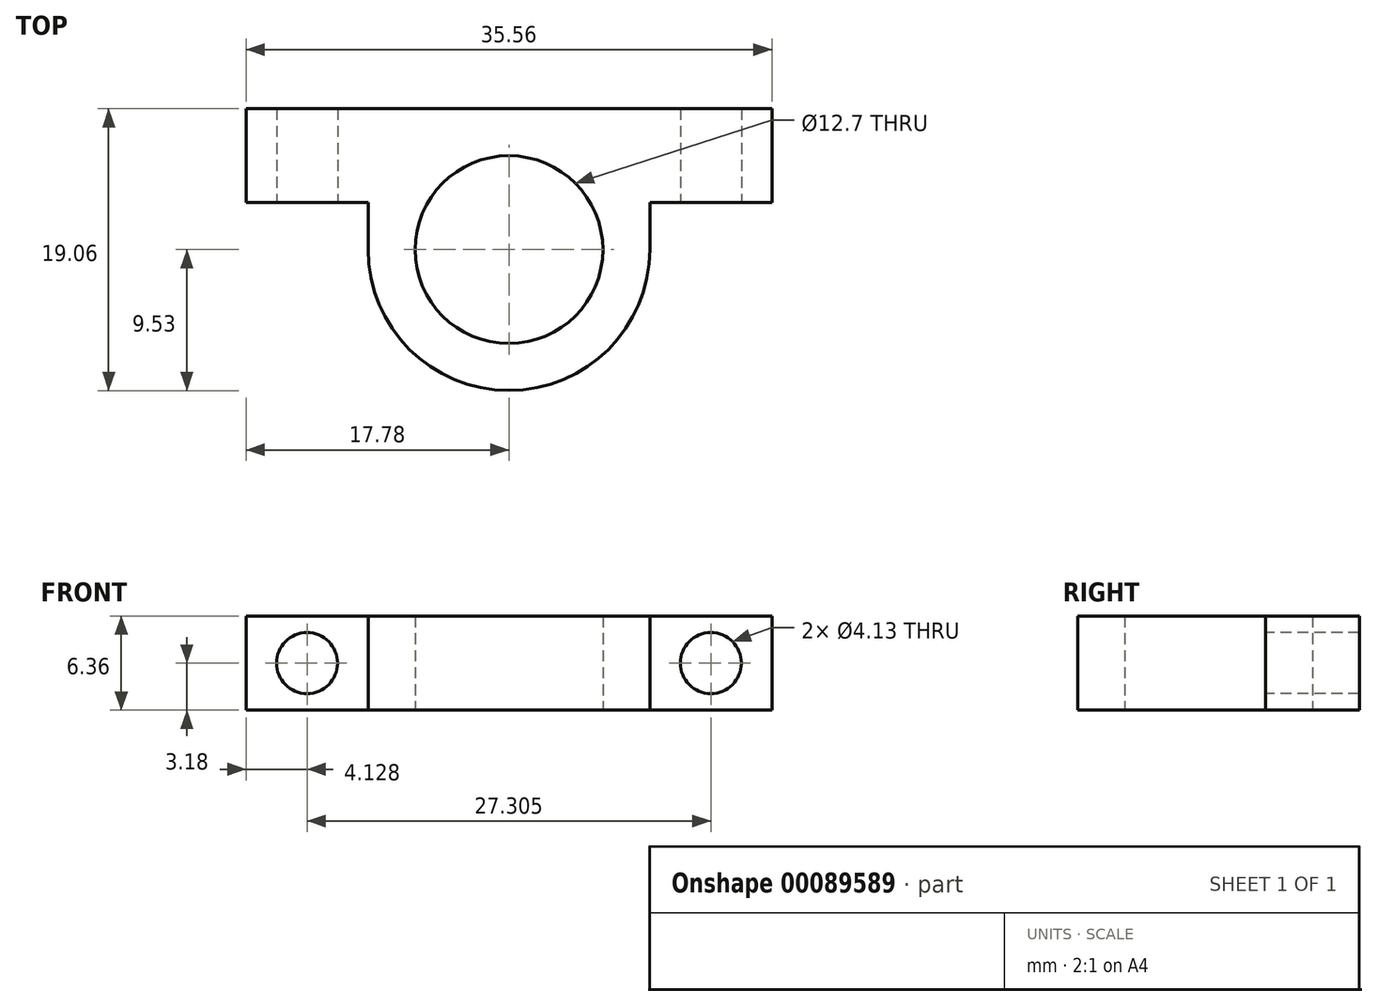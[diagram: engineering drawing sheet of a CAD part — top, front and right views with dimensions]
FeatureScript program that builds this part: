
annotation { "Feature Type Name" : "Feature", "Feature Type Description" : "" }
export const myFeature = defineFeature(function(context is Context, id is Id, definition is map)
    precondition{}
    {
        {
            var Q0;
            Q0=qCreatedBy(makeId("Top.planeOp"),FACE);
            var sketch = newSketch(context, id + "F0", { "sketchPlane" : qUnion([Q0])});
            skCircle(sketch, "E0", {"center": v(0, 0) * mm, "radius": 6.35 * mm});
            skArc(sketch, "E1", {"start": v(-9.53, 0) * mm, "mid": v(0, -9.53) * mm, "end": v(9.53, 0) * mm});
            skLineSegment(sketch, "E2", {"start": v(-9.53, 0) * mm, "end": v(-9.53, 3.17) * mm});
            skLineSegment(sketch, "E3", {"start": v(-9.53, 3.17) * mm, "end": v(-17.78, 3.17) * mm});
            skLineSegment(sketch, "E4", {"start": v(-17.78, 3.17) * mm, "end": v(-17.78, 9.53) * mm});
            skLineSegment(sketch, "E5.MirrorCS", {"start": v(17.78, 3.17) * mm, "end": v(17.78, 9.53) * mm});
            skLineSegment(sketch, "E6.MirrorCS", {"start": v(9.53, 3.18) * mm, "end": v(17.78, 3.18) * mm});
            skLineSegment(sketch, "E7.MirrorCS", {"start": v(9.53, 0) * mm, "end": v(9.53, 3.17) * mm});
            skLineSegment(sketch, "E8", {"start": v(-17.78, 9.52) * mm, "end": v(17.78, 9.53) * mm});
            skPoint(sketch, "E9", {"position": v(-9.53, 9.52) * mm});
            skPoint(sketch, "E10", {"position": v(-13.65, 9.52) * mm});
            skPoint(sketch, "E10.positionSnap0", {"position": v(-13.65, 3.17) * mm});
            skPoint(sketch, "E11", {"position": v(13.65, 9.53) * mm});
            skPoint(sketch, "E11.positionSnap0", {"position": v(13.65, 3.18) * mm});
            skSolve(sketch);
        }
        {
            var Q0;
            Q0=makeQuery(id+"F0.imprint","IMPRINT",FACE,{"disambiguationData":[TD([[makeQuery(id+"F0.imprint","IMPRINT",EDGE,{"derivedFrom":sQuery(id+"F0.wireOp",EDGE,"E0")}),-1.0]])]});
            extrude(context, id + "F1", {"entities" : qUnion([Q0]), "endBound" : BoundingType.SYMMETRIC, "depth" : 6.35 * mm});
        }
        {
            var Q0;
            Q0=makeQuery(id+"F1.opExtrude","SWEPT_FACE",FACE,{"disambiguationData":[OSD([sQuery(id+"F0.wireOp",EDGE,"E3")])]});
            var sketch = newSketch(context, id + "F2", { "sketchPlane" : qUnion([Q0])});
            skLineSegment(sketch, "E12", {"start": v(-13.65, 3.18) * mm, "end": v(-13.65, -3.18) * mm, "construction": true});
            skCircle(sketch, "E13", {"center": v(-13.65, 0) * mm, "radius": 2.06 * mm});
            skSolve(sketch);
        }
        {
            var Q0;
            Q0=qSketchRegion(id+"F2",true);
            extrude(context, id + "F3", {"entities" : qUnion([Q0]), "operationType" : NewBodyOperationType.REMOVE, "endBound" : BoundingType.THROUGH_ALL, "oppositeDirection" : true, "depth" : 25.4 * mm});
        }
        {
            var Q0;
            Q0=makeQuery(id+"F1.opExtrude","SWEPT_FACE",FACE,{"disambiguationData":[OSD([sQuery(id+"F0.wireOp",EDGE,"E6.MirrorCS")])]});
            var sketch = newSketch(context, id + "F4", { "sketchPlane" : qUnion([Q0])});
            skLineSegment(sketch, "E14", {"start": v(13.65, -3.18) * mm, "end": v(13.65, 3.18) * mm, "construction": true});
            skCircle(sketch, "E15", {"center": v(13.65, 0) * mm, "radius": 2.06 * mm});
            skSolve(sketch);
        }
        {
            var Q0;
            Q0=qSketchRegion(id+"F4",true);
            extrude(context, id + "F5", {"entities" : qUnion([Q0]), "operationType" : NewBodyOperationType.REMOVE, "endBound" : BoundingType.THROUGH_ALL, "oppositeDirection" : true, "depth" : 25.4 * mm});
        }
    });
